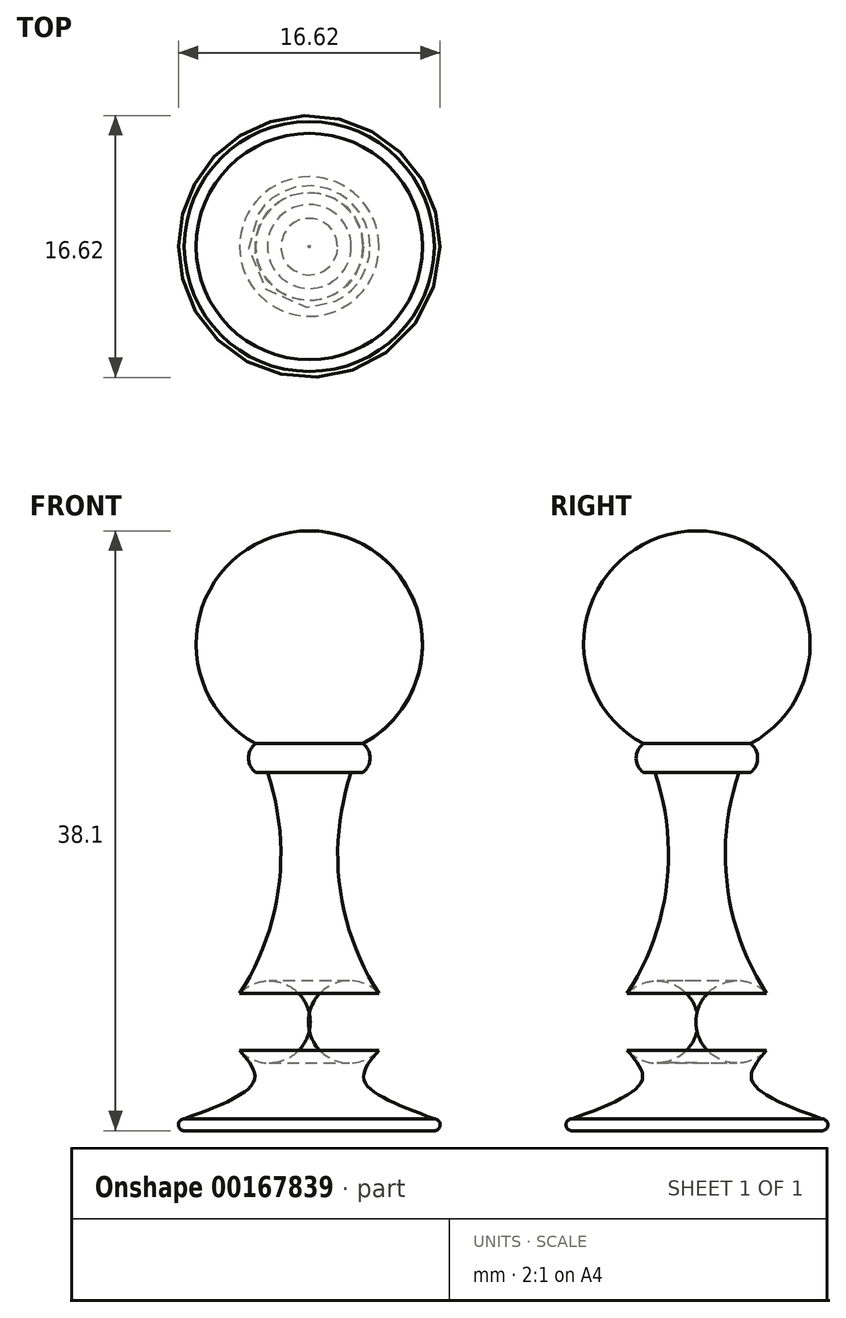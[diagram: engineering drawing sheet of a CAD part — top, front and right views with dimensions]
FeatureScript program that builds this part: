
annotation { "Feature Type Name" : "Feature", "Feature Type Description" : "" }
export const myFeature = defineFeature(function(context is Context, id is Id, definition is map)
    precondition{}
    {
        {
            var Q0;
            Q0=qCreatedBy(makeId("Front.planeOp"),FACE);
            var sketch = newSketch(context, id + "F0", { "sketchPlane" : qUnion([Q0])});
            skLineSegment(sketch, "E0", {"start": v(0, 38.1) * mm, "end": v(0, 0) * mm});
            skLineSegment(sketch, "E1", {"start": v(0, 0) * mm, "end": v(7.94, 0) * mm});
            skArc(sketch, "E2", {"start": v(3.4, 24.58) * mm, "mid": v(6.97, 32.67) * mm, "end": v(0, 38.1) * mm});
            skArc(sketch, "E3", {"start": v(2.67, 22.76) * mm, "mid": v(1.93, 15.54) * mm, "end": v(4.43, 8.71) * mm});
            skArc(sketch, "E4", {"start": v(4.43, 5.1) * mm, "mid": v(5.16, 6.9) * mm, "end": v(4.43, 8.71) * mm});
            skArc(sketch, "E5", {"start": v(3.4, 22.76) * mm, "mid": v(3.86, 23.67) * mm, "end": v(3.4, 24.58) * mm});
            skLineSegment(sketch, "E6", {"start": v(3.4, 22.76) * mm, "end": v(2.67, 22.76) * mm});
            skArc(sketch, "E7", {"start": v(7.94, 0) * mm, "mid": v(8.31, 0.38) * mm, "end": v(7.94, 0.75) * mm});
            skFitSpline(sketch, "E8", {"points": [v(4.43, 5.1) * mm, v(3.48, 3.2) * mm, v(7.94, 0.75) * mm], "startDerivative": vector(-4.32, -4.97) * mm, "endDerivative": vector(10.28, -3.8) * mm});
            skSolve(sketch);
        }
        {
            var Q0;
            Q0 = qSketchRegion(id + "F0", true);
            var Q1;
            Q1=sQuery(id+"F0.wireOp",EDGE,"E0");
            revolve(context, id + "F1", {"entities" : qUnion([Q0]), "axis" : qUnion([Q1]), "revolveType" : RevolveType.FULL});
        }
    });
